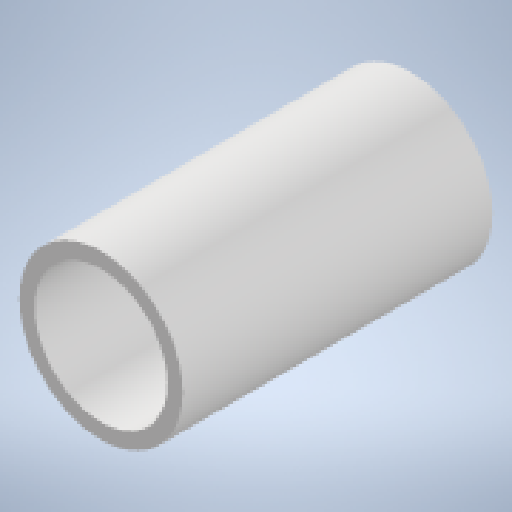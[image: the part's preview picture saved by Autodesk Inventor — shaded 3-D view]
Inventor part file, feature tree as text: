
AUTODESK INVENTOR PART (.ipt)
format: ipt  version: 2023.1 (Build 271208000, 208)  size: 141,312 bytes
history: native  units: mm
features: revolve x1, sketch x1
ambient origin geometry x8: Origin, YZ Plane, XZ Plane, XY Plane, X Axis, Y Axis, Z Axis, Center Point
bodies: Solid1 (feature_tree)
feature tree (2):
  revolve  "Revolution1"  [1 undecoded]
  sketch  "Sketch1"  dims[d0=2.0mm d1=40.4mm d2=21.3mm d3=90.0deg]
note: 1 required parameter value undecoded (feature->parameter linkage not recoverable at this tier; creation-order binding heuristic only, values carry confidence <= 0.55)
